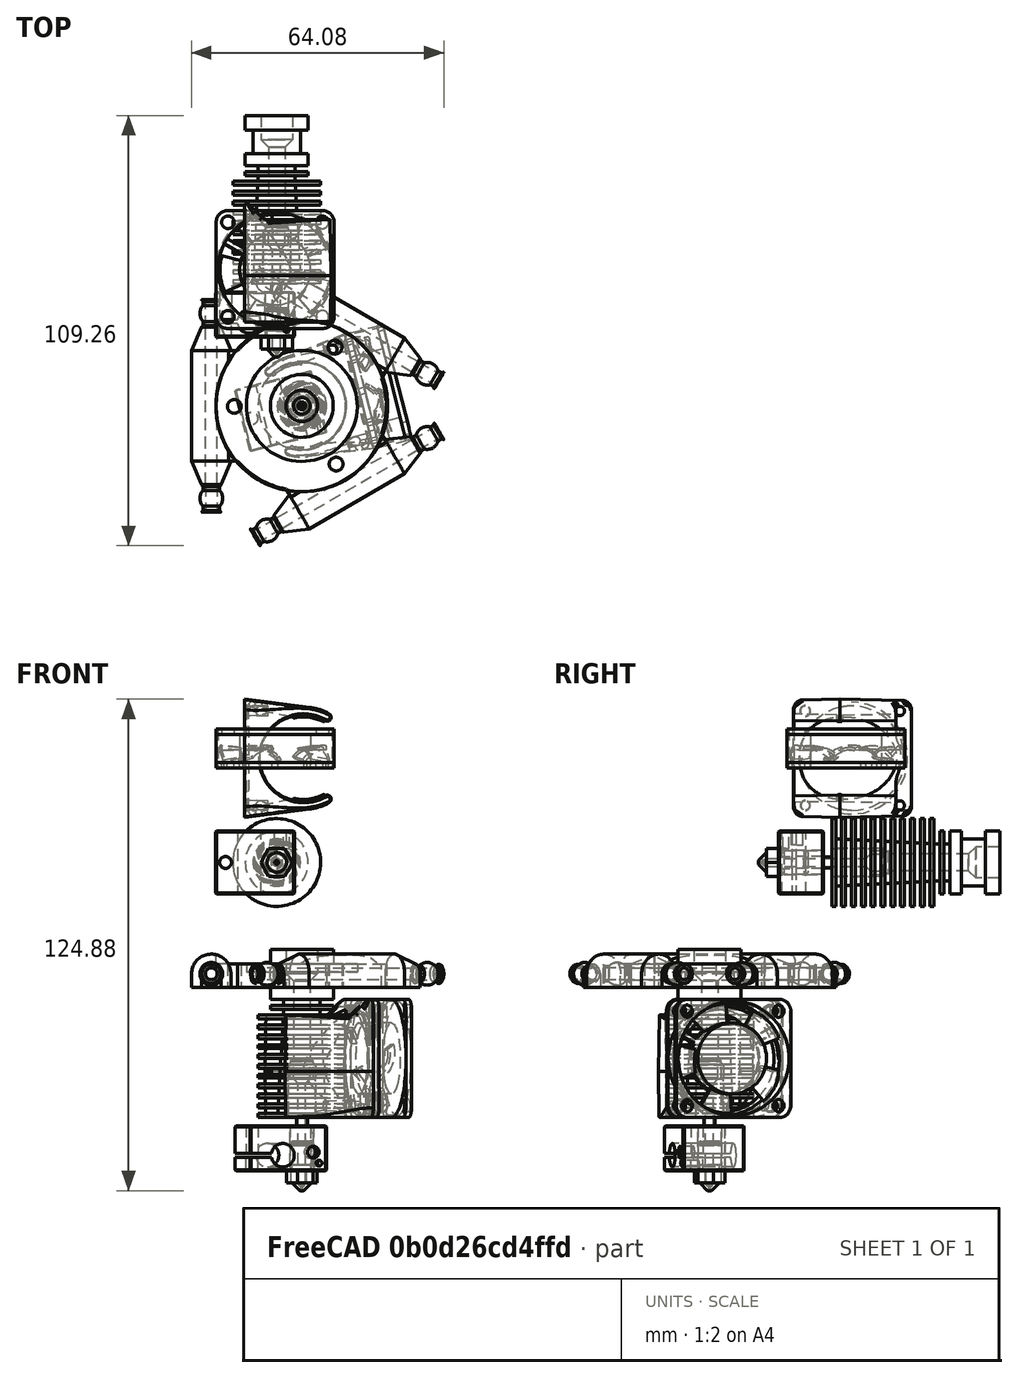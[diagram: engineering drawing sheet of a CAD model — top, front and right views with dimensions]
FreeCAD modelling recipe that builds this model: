
FCSTD DOCUMENT  (FreeCAD 2022.118R30769 (Git))
Label: effector_part
License: All rights reserved
LicenseURL: http://en.wikipedia.org/wiki/All_rights_reserved
objects: Part::FeaturePython×30, App::FeaturePython×27, Part::Feature×8, App::LinkElement×6, App::Part×3, App::Link×2
note: 36 computed .brp shape members not serialized (recipe doc carries the construction recipe); baked Part::Feature solids carry a one-line shape summary decoded from their .brp
EXTERNAL_REF file=Traxxas 5347 ball joint.FCStd obj=Assembly

FEATURE [App::FeaturePython] Constraints001  # WARN: FeaturePython — macro-defined, semantics opaque (R4)
  TreeRank = 258
  _LinkVersion = 1
  _Version = 1
FEATURE [Part::Feature] Solid  label="e3d nozzle (0.4)"
  Placement = pos=(0,-4.25,4e-16) rot=(0,0,1;0rad)
  TreeRank = 195
  shape: bbox 8.083 x 12.5 x 7 mm, 31 faces (baked)
FEATURE [Part::Feature] Solid001  label="e3d heaterblock"
  Placement = pos=(-5.5,-1.25,6.9e-15) rot=(0,0,1;0rad)
  TreeRank = 196
  shape: bbox 20 x 11.5 x 16 mm, 45 faces (baked)
FEATURE [Part::Feature] Solid002  label="e3d heat break"
  Placement = pos=(0,5.25,4e-16) rot=(0,0,1;0rad)
  TreeRank = 197
  shape: bbox 7 x 21.9 x 7 mm, 23 faces (baked)
FEATURE [Part::Feature] Solid003  label="e3d heatsink"
  Placement = pos=(0,12.35,4e-16) rot=(0,1,0;0.209118rad)
  TreeRank = 198
  shape: bbox 22.3 x 42.7 x 22.3 mm, 92 faces (baked)
FEATURE [Part::Feature] Solid004  label="fan duct"
  Placement = pos=(6.82793,2.62156,26.4875) rot=(0,0,1;0rad)
  TreeRank = 199
  shape: bbox 55.54 x 30 x 38.08 mm, 106 faces (baked)
FEATURE [Part::Feature] Solid005  label="fan sub1"
  Placement = pos=(-0.402046,15.9429,23.9537) rot=(0,0,1;0rad)
  TreeRank = 200
  shape: bbox 30 x 30 x 10 mm, 57 faces (baked)
FEATURE [Part::Feature] Solid006  label="fan sub2"
  Placement = pos=(-0.402046,15.9429,33.9537) rot=(-0.381664,-0.841822,-0.381664;1.74214rad)
  TreeRank = 201
  shape: bbox 29.15 x 29.85 x 8.5 mm, 30 faces (baked)
FEATURE [App::Part] Part  label="fan"
  ExportMode = 1
  Group = -> [Solid005,Solid006]
  Origin = -> Origin001
  Placement = pos=(15.7816,1.67867,26.8895) rot=(0,-1,0;1.5708rad)
  TreeRank = 203
  _ExportChildren = -> [Solid005,Solid006]
  _GroupVersion = 1
FEATURE [App::Part] Part001  label="fanduct"
  ExportMode = 1
  Group = -> [Solid004,Part]
  Origin = -> Origin002
  Placement = pos=(6.82793,9.72844,26.4875) rot=(0,1,0;3.14159rad)
  TreeRank = 205
  _ExportChildren = -> [Solid004,Part]
  _GroupVersion = 1
FEATURE [App::Part] Part002  label="e3d v6"
  ExportMode = 1
  Group = -> [Solid,Solid001,Solid002,Solid003,Part001]
  Origin = -> Origin003
  Placement = pos=(65.8913,-6.33526,94.8) rot=(1,0.000157,0.000157;1.5708rad)
  TreeRank = 207
  _ExportChildren = -> [Solid,Solid001,Solid002,Solid003,Part001]
  _GroupVersion = 1
FEATURE [Part::FeaturePython] Parts001  # WARN: FeaturePython — macro-defined, semantics opaque (R4)
  Group = -> [Part002]
  GroupMode = 0
  TreeRank = 260
  _LinkVersion = 1
FEATURE [App::Link] Link001  label="AsE3dv007"
  AutoLinkLabel = false
  AutoPlacement = true
  LinkPlacement = pos=(-59.0731,-28.6152,-171.944) rot=(0,0,1;0.246235rad)
  LinkedObject = -> Assembly001
  Placement = pos=(-59.0731,-28.6152,-171.944) rot=(0,0,1;0.246235rad)
  SyncGroupVisibility = false
  TreeRank = 0
  _LinkOwner = 965
  _LinkVersion = 1
FEATURE [Part::Feature] Part__Feature044  label="Delta Effector"
  Placement = pos=(-5.1086,-20.3772,-4.35843) rot=(0,0,1;1.13446rad)
  TreeRank = 0
  shape: bbox 58.07 x 64.17 x 8.5 mm, 53 faces (baked)
FEATURE [App::LinkElement] Link_i0
  LinkPlacement = pos=(-16.625,-42.188,-28.294) rot=(0,0,-1;1.5708rad)
  LinkedObject = -> <external Traxxas 5347 ball joint.FCStd>#Assembly
  Placement = pos=(-16.625,-42.188,-28.294) rot=(0,0,-1;1.5708rad)
  TreeRank = 265
  _LinkOwner = 548
  _LinkVersion = 1
FEATURE [App::LinkElement] Link_i1
  LinkPlacement = pos=(-16.625,4.79197,-28.294) rot=(0,0,-1;4.71239rad)
  LinkedObject = -> <external Traxxas 5347 ball joint.FCStd>#Assembly
  Placement = pos=(-16.625,4.79197,-28.294) rot=(0,0,-1;4.71239rad)
  TreeRank = 266
  _LinkOwner = 548
  _LinkVersion = 1
FEATURE [App::LinkElement] Link_i2
  LinkPlacement = pos=(-2.46794,12.9656,-28.294) rot=(0,0,-1;3.66519rad)
  LinkedObject = -> <external Traxxas 5347 ball joint.FCStd>#Assembly
  Placement = pos=(-2.46794,12.9656,-28.294) rot=(0,0,-1;3.66519rad)
  TreeRank = 267
  _LinkOwner = 548
  _LinkVersion = 1
FEATURE [App::LinkElement] Link_i3
  LinkPlacement = pos=(38.2179,-10.5244,-28.294) rot=(0,0,-1;0.523599rad)
  LinkedObject = -> <external Traxxas 5347 ball joint.FCStd>#Assembly
  Placement = pos=(38.2179,-10.5244,-28.294) rot=(0,0,-1;0.523599rad)
  TreeRank = 268
  _LinkOwner = 548
  _LinkVersion = 1
FEATURE [App::LinkElement] Link_i4
  LinkPlacement = pos=(38.2179,-26.8716,-28.294) rot=(0,0,1;0.523599rad)
  LinkedObject = -> <external Traxxas 5347 ball joint.FCStd>#Assembly
  Placement = pos=(38.2179,-26.8716,-28.294) rot=(0,0,1;0.523599rad)
  TreeRank = 269
  _LinkOwner = 548
  _LinkVersion = 1
FEATURE [App::LinkElement] Link_i5
  LinkPlacement = pos=(-2.46794,-50.3616,-28.294) rot=(0,0,-1;2.61799rad)
  LinkedObject = -> <external Traxxas 5347 ball joint.FCStd>#Assembly
  Placement = pos=(-2.46794,-50.3616,-28.294) rot=(0,0,-1;2.61799rad)
  TreeRank = 270
  _LinkOwner = 548
  _LinkVersion = 1
FEATURE [App::Link] Link  label="As3Traxxas5347ball"
  AutoLinkLabel = false
  AutoPlacement = true
  ElementCount = 6
  ElementList = -> [Link_i0,Link_i1,Link_i2,Link_i3,Link_i4,Link_i5]
  LinkedObject = -> <external Traxxas 5347 ball joint.FCStd>#Assembly
  SyncGroupVisibility = false
  TreeRank = 264
  _LinkOwner = 534
  _LinkVersion = 1
FEATURE [Part::FeaturePython] Parts002  # WARN: FeaturePython — macro-defined, semantics opaque (R4)
  Group = -> [Part__Feature044,Link001,Link]
  GroupMode = 0
  TreeRank = 0
  _LinkVersion = 1
FEATURE [Part::FeaturePython] Assembly001  label="AsE3dv6"  # WARN: FeaturePython — macro-defined, semantics opaque (R4)
  AutoRelax = true
  BuildShape = 0
  Freeze = false
  Group = -> [Constraints001,Elements001,Parts001]
  TreeRank = 261
  Verbose = false
  _LinkVersion = 1
  _SolverType = 1
  _Version = 1
FEATURE [App::FeaturePython] Elements001  # WARN: FeaturePython — macro-defined, semantics opaque (R4)
  Group = -> [Element005]
  TreeRank = 259
  _LinkVersion = 1
FEATURE [Part::FeaturePython] Assembly002  label="As3DeltaEffector"  # WARN: FeaturePython — macro-defined, semantics opaque (R4)
  AutoRelax = true
  BuildShape = 0
  Freeze = true
  Group = -> [Constraints002,Elements002,Parts002]
  TreeRank = 263
  Verbose = false
  _LinkVersion = 1
  _SolverType = 1
  _Version = 1
FEATURE [App::FeaturePython] Constraint  label="Locked"  # WARN: FeaturePython — macro-defined, semantics opaque (R4)
  Disabled = false
  Group = -> [ElementLink]
  TreeRank = 0
  _ConstraintType = 0
  _LinkVersion = 1
  _Parent = -> Constraints002
FEATURE [App::FeaturePython] Constraint001  label="PlaneCoincident"  # WARN: FeaturePython — macro-defined, semantics opaque (R4)
  Angle = 0
  AnglePitch = 0
  AngleRoll = 0
  Cascade = false
  Disabled = false
  Group = -> [ElementLink001,ElementLink002]
  LockAngle = false
  Multiply = false
  OffsetX = 0
  OffsetY = 0
  TreeRank = 0
  _ConstraintType = 35
  _LinkVersion = 1
  _Parent = -> Constraints002
FEATURE [App::FeaturePython] Constraint002  label="PlaneCoincident001"  # WARN: FeaturePython — macro-defined, semantics opaque (R4)
  Angle = 0
  AnglePitch = 0
  AngleRoll = 0
  Cascade = false
  Disabled = false
  Group = -> [ElementLink003,ElementLink004]
  LockAngle = false
  Multiply = false
  OffsetX = 0
  OffsetY = 0
  TreeRank = 0
  _ConstraintType = 35
  _LinkVersion = 1
  _Parent = -> Constraints002
FEATURE [App::FeaturePython] Constraint003  label="PlaneCoincident002"  # WARN: FeaturePython — macro-defined, semantics opaque (R4)
  Angle = 0
  AnglePitch = 0
  AngleRoll = 0
  Cascade = false
  Disabled = false
  Group = -> [ElementLink005,ElementLink006]
  LockAngle = false
  Multiply = false
  OffsetX = 0
  OffsetY = 0
  TreeRank = 0
  _ConstraintType = 35
  _LinkVersion = 1
  _Parent = -> Constraints002
FEATURE [App::FeaturePython] Constraint004  label="PlaneCoincident003"  # WARN: FeaturePython — macro-defined, semantics opaque (R4)
  Angle = 0
  AnglePitch = 0
  AngleRoll = 0
  Cascade = false
  Disabled = false
  Group = -> [ElementLink007,ElementLink008]
  LockAngle = false
  Multiply = false
  OffsetX = 0
  OffsetY = 0
  TreeRank = 0
  _ConstraintType = 35
  _LinkVersion = 1
  _Parent = -> Constraints002
FEATURE [App::FeaturePython] Constraint005  label="PlaneCoincident004"  # WARN: FeaturePython — macro-defined, semantics opaque (R4)
  Angle = 0
  AnglePitch = 0
  AngleRoll = 0
  Cascade = false
  Disabled = false
  Group = -> [ElementLink009,ElementLink010]
  LockAngle = false
  Multiply = false
  OffsetX = 0
  OffsetY = 0
  TreeRank = 0
  _ConstraintType = 35
  _LinkVersion = 1
  _Parent = -> Constraints002
FEATURE [App::FeaturePython] Constraint006  label="PlaneCoincident005"  # WARN: FeaturePython — macro-defined, semantics opaque (R4)
  Angle = 0
  AnglePitch = 0
  AngleRoll = 0
  Cascade = false
  Disabled = false
  Group = -> [ElementLink011,ElementLink012]
  LockAngle = false
  Multiply = false
  OffsetX = 0
  OffsetY = 0
  TreeRank = 0
  _ConstraintType = 35
  _LinkVersion = 1
  _Parent = -> Constraints002
FEATURE [App::FeaturePython] Constraints002  # WARN: FeaturePython — macro-defined, semantics opaque (R4)
  Group = -> [Constraint,Constraint001,Constraint002,Constraint003,Constraint004,Constraint005,Constraint006,Constraint007]
  TreeRank = 0
  _LinkVersion = 1
  _Version = 1
FEATURE [Part::FeaturePython] Element  label="ElSphereM@As3Traxxas5347ball@#3"  # link proxy (typed FeaturePython)
  Detach = false
  LinkTransform = true
  LinkedObject = -> Link [Link_i3.1.$ElSphereM.]
  TreeRank = 0
  _LinkVersion = 1
  _Parent = -> Elements002
FEATURE [Part::FeaturePython] Element004  label="Element001"  # link proxy (typed FeaturePython)
  Detach = false
  LinkTransform = true
  LinkedObject = -> Part__Feature044 [Face51]
  TreeRank = 0
  _LinkVersion = 1
  _Parent = -> Elements002
FEATURE [App::FeaturePython] ElementLink  label="_Element"  # link proxy (typed FeaturePython)
  LinkTransform = true
  LinkedObject = -> _Element
  TreeRank = 0
  _LinkVersion = 1
  _Parent = -> Constraint
FEATURE [App::FeaturePython] ElementLink001  label="ElCircle@As3Traxxas5347ball@#0"  # link proxy (typed FeaturePython)
  LinkTransform = true
  LinkedObject = -> _Element001
  TreeRank = 0
  _LinkVersion = 1
  _Parent = -> Constraint001
FEATURE [App::FeaturePython] ElementLink002  label="_Element002"  # link proxy (typed FeaturePython)
  LinkTransform = true
  LinkedObject = -> _Element002
  TreeRank = 0
  _LinkVersion = 1
  _Parent = -> Constraint001
FEATURE [App::FeaturePython] ElementLink003  label="ElCircle@As3Traxxas5347ball@#1"  # link proxy (typed FeaturePython)
  LinkTransform = true
  LinkedObject = -> _Element003
  TreeRank = 0
  _LinkVersion = 1
  _Parent = -> Constraint002
FEATURE [App::FeaturePython] ElementLink004  label="_Element004"  # link proxy (typed FeaturePython)
  LinkTransform = true
  LinkedObject = -> _Element004
  TreeRank = 0
  _LinkVersion = 1
  _Parent = -> Constraint002
FEATURE [App::FeaturePython] ElementLink005  label="ElCircle@As3Traxxas5347ball@#2"  # link proxy (typed FeaturePython)
  LinkTransform = true
  LinkedObject = -> _Element005
  TreeRank = 0
  _LinkVersion = 1
  _Parent = -> Constraint003
FEATURE [App::FeaturePython] ElementLink006  label="_Element006"  # link proxy (typed FeaturePython)
  LinkTransform = true
  LinkedObject = -> _Element006
  TreeRank = 0
  _LinkVersion = 1
  _Parent = -> Constraint003
FEATURE [App::FeaturePython] ElementLink007  label="ElCircle@As3Traxxas5347ball@#3"  # link proxy (typed FeaturePython)
  LinkTransform = true
  LinkedObject = -> _Element007
  TreeRank = 0
  _LinkVersion = 1
  _Parent = -> Constraint004
FEATURE [App::FeaturePython] ElementLink008  label="_Element008"  # link proxy (typed FeaturePython)
  LinkTransform = true
  LinkedObject = -> _Element008
  TreeRank = 0
  _LinkVersion = 1
  _Parent = -> Constraint004
FEATURE [App::FeaturePython] ElementLink009  label="ElCircle@As3Traxxas5347ball@#4"  # link proxy (typed FeaturePython)
  LinkTransform = true
  LinkedObject = -> _Element009
  TreeRank = 0
  _LinkVersion = 1
  _Parent = -> Constraint005
FEATURE [App::FeaturePython] ElementLink010  label="_Element010"  # link proxy (typed FeaturePython)
  LinkTransform = true
  LinkedObject = -> _Element010
  TreeRank = 0
  _LinkVersion = 1
  _Parent = -> Constraint005
FEATURE [App::FeaturePython] ElementLink011  label="ElCircle@As3Traxxas5347ball@#5"  # link proxy (typed FeaturePython)
  LinkTransform = true
  LinkedObject = -> _Element011
  TreeRank = 0
  _LinkVersion = 1
  _Parent = -> Constraint006
FEATURE [App::FeaturePython] ElementLink012  label="_Element012"  # link proxy (typed FeaturePython)
  LinkTransform = true
  LinkedObject = -> _Element012
  TreeRank = 0
  _LinkVersion = 1
  _Parent = -> Constraint006
FEATURE [App::FeaturePython] Elements002  # WARN: FeaturePython — macro-defined, semantics opaque (R4)
  Group = -> [_Element,_Element001,_Element002,_Element003,_Element004,_Element005,_Element006,_Element007,_Element008,_Element009,_Element010,_Element011,_Element012,Element,Element004,_Element013,_Element014,Element006,Element007,Element008,Element009,Element010,Element011,Element012,Element013]
  TreeRank = 0
  _LinkVersion = 1
FEATURE [Part::FeaturePython] _Element  # link proxy (typed FeaturePython)
  Detach = false
  LinkTransform = true
  LinkedObject = -> Part__Feature044 [Face50]
  TreeRank = 0
  _LinkVersion = 1
  _Parent = -> Elements002
FEATURE [Part::FeaturePython] _Element001  label="ElCircle@As3Traxxas5347ball@#0"  # link proxy (typed FeaturePython)
  Detach = false
  LinkTransform = true
  LinkedObject = -> Link [Link_i0.1.$ElCircle.]
  TreeRank = 0
  _LinkVersion = 1
  _Parent = -> Elements002
FEATURE [Part::FeaturePython] _Element002  # link proxy (typed FeaturePython)
  Detach = false
  LinkTransform = true
  LinkedObject = -> Part__Feature044 [Edge45]
  TreeRank = 0
  _LinkVersion = 1
  _Parent = -> Elements002
FEATURE [Part::FeaturePython] _Element003  label="ElCircle@As3Traxxas5347ball@#1"  # link proxy (typed FeaturePython)
  Detach = false
  LinkTransform = true
  LinkedObject = -> Link [Link_i1.1.$ElCircle.]
  TreeRank = 0
  _LinkVersion = 1
  _Parent = -> Elements002
FEATURE [Part::FeaturePython] _Element004  # link proxy (typed FeaturePython)
  Detach = false
  LinkTransform = true
  LinkedObject = -> Part__Feature044 [Edge44]
  TreeRank = 0
  _LinkVersion = 1
  _Parent = -> Elements002
FEATURE [Part::FeaturePython] _Element005  label="ElCircle@As3Traxxas5347ball@#2"  # link proxy (typed FeaturePython)
  Detach = false
  LinkTransform = true
  LinkedObject = -> Link [Link_i2.1.$ElCircle.]
  TreeRank = 0
  _LinkVersion = 1
  _Parent = -> Elements002
FEATURE [Part::FeaturePython] _Element006  # link proxy (typed FeaturePython)
  Detach = false
  LinkTransform = true
  LinkedObject = -> Part__Feature044 [Edge37]
  TreeRank = 0
  _LinkVersion = 1
  _Parent = -> Elements002
FEATURE [Part::FeaturePython] _Element007  label="ElCircle@As3Traxxas5347ball@#3"  # link proxy (typed FeaturePython)
  Detach = false
  LinkTransform = true
  LinkedObject = -> Link [Link_i3.1.$ElCircle.]
  TreeRank = 0
  _LinkVersion = 1
  _Parent = -> Elements002
FEATURE [Part::FeaturePython] _Element008  # link proxy (typed FeaturePython)
  Detach = false
  LinkTransform = true
  LinkedObject = -> Part__Feature044 [Edge36]
  TreeRank = 0
  _LinkVersion = 1
  _Parent = -> Elements002
FEATURE [Part::FeaturePython] _Element009  label="ElCircle@As3Traxxas5347ball@#4"  # link proxy (typed FeaturePython)
  Detach = false
  LinkTransform = true
  LinkedObject = -> Link [Link_i4.1.$ElCircle.]
  TreeRank = 0
  _LinkVersion = 1
  _Parent = -> Elements002
FEATURE [Part::FeaturePython] _Element010  # link proxy (typed FeaturePython)
  Detach = false
  LinkTransform = true
  LinkedObject = -> Part__Feature044 [Edge24]
  TreeRank = 0
  _LinkVersion = 1
  _Parent = -> Elements002
FEATURE [Part::FeaturePython] _Element011  label="ElCircle@As3Traxxas5347ball@#5"  # link proxy (typed FeaturePython)
  Detach = false
  LinkTransform = true
  LinkedObject = -> Link [Link_i5.1.$ElCircle.]
  TreeRank = 0
  _LinkVersion = 1
  _Parent = -> Elements002
FEATURE [Part::FeaturePython] _Element012  # link proxy (typed FeaturePython)
  Detach = false
  LinkTransform = true
  LinkedObject = -> Part__Feature044 [Edge23]
  TreeRank = 0
  _LinkVersion = 1
  _Parent = -> Elements002
FEATURE [App::FeaturePython] Constraint007  label="PlaneCoincident006"  # WARN: FeaturePython — macro-defined, semantics opaque (R4)
  Angle = 0
  AnglePitch = 0
  AngleRoll = 0
  Cascade = false
  Disabled = false
  Group = -> [ElementLink013,ElementLink014]
  LockAngle = false
  Multiply = false
  OffsetX = 0
  OffsetY = 0
  TreeRank = 271
  _ConstraintType = 35
  _LinkVersion = 1
  _Parent = -> Constraints002
FEATURE [App::FeaturePython] ElementLink013  label="_Element013"  # link proxy (typed FeaturePython)
  LinkTransform = true
  LinkedObject = -> _Element013
  TreeRank = 272
  _LinkVersion = 1
  _Parent = -> Constraint007
FEATURE [Part::FeaturePython] _Element013  # link proxy (typed FeaturePython)
  Detach = false
  LinkTransform = true
  LinkedObject = -> Part__Feature044 [Edge136]
  TreeRank = 273
  _LinkVersion = 1
  _Parent = -> Elements002
FEATURE [App::FeaturePython] ElementLink014  label="_Element014"  # link proxy (typed FeaturePython)
  LinkTransform = true
  LinkedObject = -> _Element014
  TreeRank = 274
  _LinkVersion = 1
  _Parent = -> Constraint007
FEATURE [Part::FeaturePython] Element005  # link proxy (typed FeaturePython)
  Detach = false
  LinkTransform = true
  LinkedObject = -> Part002 [Solid003.Edge147]
  TreeRank = 275
  _LinkVersion = 1
  _Parent = -> Elements001
FEATURE [Part::FeaturePython] _Element014  # link proxy (typed FeaturePython)
  Detach = false
  LinkTransform = true
  LinkedObject = -> Link001 [1.$Element005.]
  TreeRank = 276
  _LinkVersion = 1
  _Parent = -> Elements002
FEATURE [Part::FeaturePython] Element006  label="ElSphereM@As3Traxxas5347ball@#0"  # link proxy (typed FeaturePython)
  Detach = false
  LinkTransform = true
  LinkedObject = -> Link [Link_i0.1.$ElSphereM.]
  TreeRank = 277
  _LinkVersion = 1
  _Parent = -> Elements002
FEATURE [Part::FeaturePython] Element007  label="ElSphereM@As3Traxxas5347ball@#1"  # link proxy (typed FeaturePython)
  Detach = false
  LinkTransform = true
  LinkedObject = -> Link [Link_i1.1.$ElSphereM.]
  TreeRank = 278
  _LinkVersion = 1
  _Parent = -> Elements002
FEATURE [Part::FeaturePython] Element008  label="ElSphereM@As3Traxxas5347ball@#2"  # link proxy (typed FeaturePython)
  Detach = false
  LinkTransform = true
  LinkedObject = -> Link [Link_i2.1.$ElSphereM.]
  TreeRank = 279
  _LinkVersion = 1
  _Parent = -> Elements002
FEATURE [Part::FeaturePython] Element009  label="ElSphereM@As3Traxxas5347ball@#4"  # link proxy (typed FeaturePython)
  Detach = false
  LinkTransform = true
  LinkedObject = -> Link [Link_i4.1.$ElSphereM.]
  TreeRank = 280
  _LinkVersion = 1
  _Parent = -> Elements002
FEATURE [Part::FeaturePython] Element010  label="ElSphereM@As3Traxxas5347ball@#5"  # link proxy (typed FeaturePython)
  Detach = false
  LinkTransform = true
  LinkedObject = -> Link [Link_i5.1.$ElSphereM.]
  TreeRank = 281
  _LinkVersion = 1
  _Parent = -> Elements002
FEATURE [Part::FeaturePython] Element011  # link proxy (typed FeaturePython)
  Detach = false
  LinkTransform = true
  LinkedObject = -> Link [1.1.$Element007.]
  TreeRank = 282
  _LinkVersion = 1
  _Parent = -> Elements002
FEATURE [Part::FeaturePython] Element012  # link proxy (typed FeaturePython)
  Detach = false
  LinkTransform = true
  LinkedObject = -> Link [0.1.$Element007.]
  TreeRank = 283
  _LinkVersion = 1
  _Parent = -> Elements002
FEATURE [Part::FeaturePython] Element013  # link proxy (typed FeaturePython)
  Detach = false
  LinkTransform = true
  LinkedObject = -> Part__Feature044 [Edge135]
  TreeRank = 284
  _LinkVersion = 1
  _Parent = -> Elements002
